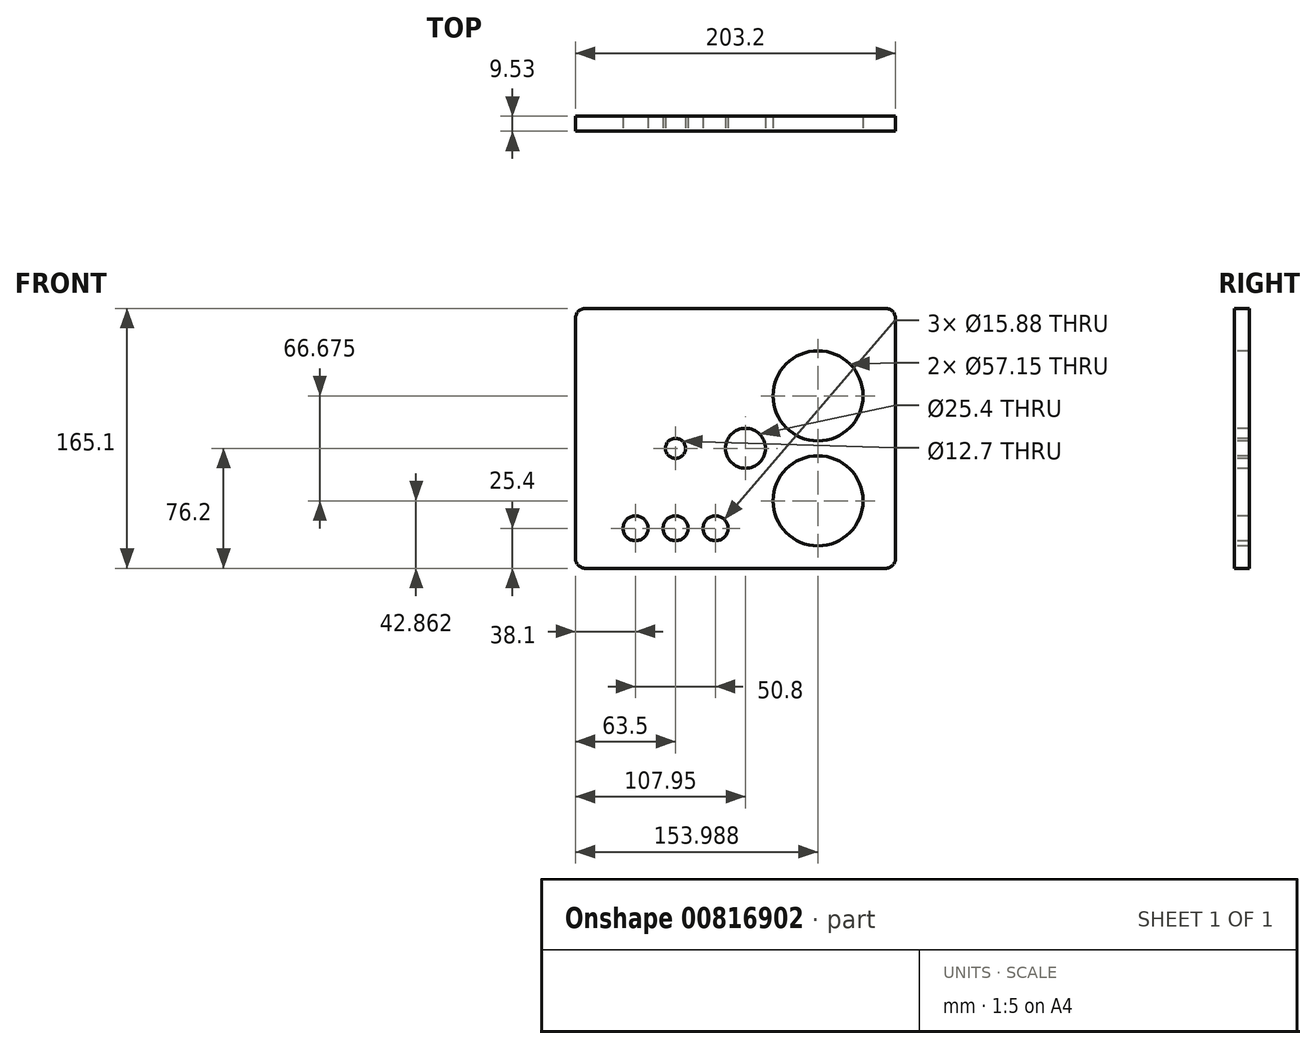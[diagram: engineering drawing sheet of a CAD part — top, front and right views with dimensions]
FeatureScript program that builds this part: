
annotation { "Feature Type Name" : "Feature", "Feature Type Description" : "" }
export const myFeature = defineFeature(function(context is Context, id is Id, definition is map)
    precondition{}
    {
        {
            var Q0;
            Q0=qCreatedBy(makeId("Front.planeOp"),FACE);
            var sketch = newSketch(context, id + "F0", { "sketchPlane" : qUnion([Q0])});
            skLineSegment(sketch, "E0.bottom", {"start": v(95.25, -82.55) * mm, "end": v(-95.25, -82.55) * mm});
            skLineSegment(sketch, "E0.top", {"start": v(95.25, 82.55) * mm, "end": v(-95.25, 82.55) * mm});
            skLineSegment(sketch, "E0.left", {"start": v(101.6, -76.2) * mm, "end": v(101.6, 76.2) * mm});
            skLineSegment(sketch, "E0.right", {"start": v(-101.6, -76.2) * mm, "end": v(-101.6, 76.2) * mm});
            skPoint(sketch, "E0.middle", {"position": v(0, 0) * mm});
            skPoint(sketch, "E1.visualSharp", {"position": v(-101.6, 82.55) * mm});
            skArc(sketch, "E1.filletArc", {"start": v(-95.25, 82.55) * mm, "mid": v(-99.74, 80.7) * mm, "end": v(-101.6, 76.2) * mm});
            skPoint(sketch, "E2.visualSharp", {"position": v(-101.6, -82.55) * mm});
            skArc(sketch, "E2.filletArc", {"start": v(-101.6, -76.2) * mm, "mid": v(-99.74, -80.7) * mm, "end": v(-95.25, -82.55) * mm});
            skPoint(sketch, "E3.visualSharp", {"position": v(101.6, -82.55) * mm});
            skArc(sketch, "E3.filletArc", {"start": v(95.25, -82.55) * mm, "mid": v(99.74, -80.7) * mm, "end": v(101.6, -76.2) * mm});
            skPoint(sketch, "E4.visualSharp", {"position": v(101.6, 82.55) * mm});
            skArc(sketch, "E4.filletArc", {"start": v(101.6, 76.2) * mm, "mid": v(99.74, 80.7) * mm, "end": v(95.25, 82.55) * mm});
            skLineSegment(sketch, "E5.bottom", {"start": v(-88.9, 44.45) * mm, "end": v(88.9, 44.45) * mm, "construction": true});
            skLineSegment(sketch, "E5.top", {"start": v(-88.9, -69.85) * mm, "end": v(88.9, -69.85) * mm, "construction": true});
            skLineSegment(sketch, "E5.left", {"start": v(-88.9, 44.45) * mm, "end": v(-88.9, -69.85) * mm, "construction": true});
            skLineSegment(sketch, "E5.right", {"start": v(88.9, 44.45) * mm, "end": v(88.9, -69.85) * mm, "construction": true});
            skSolve(sketch);
        }
        {
            var Q0;
            Q0 = qSketchRegion(id + "F0", true);
            extrude(context, id + "F1", {"entities" : qUnion([Q0]), "depth" : 9.52 * mm, "offsetDistance" : 25.4 * mm});
        }
        {
            var Q0;
            Q0=makeQuery(id+"F1.opExtrude","CAP_FACE",FACE,{"disambiguationData":[OSD([sQuery(id+"F0.wireOp",EDGE,"E0.bottom"),sQuery(id+"F0.wireOp",EDGE,"E0.top"),sQuery(id+"F0.wireOp",EDGE,"E0.left"),sQuery(id+"F0.wireOp",EDGE,"E0.right"),sQuery(id+"F0.wireOp",EDGE,"E1.filletArc"),sQuery(id+"F0.wireOp",EDGE,"E2.filletArc"),sQuery(id+"F0.wireOp",EDGE,"E3.filletArc"),sQuery(id+"F0.wireOp",EDGE,"E4.filletArc")])],"isStart":false});
            var sketch = newSketch(context, id + "F2", { "sketchPlane" : qUnion([Q0])});
            skCircle(sketch, "E6", {"center": v(52.39, -39.69) * mm, "radius": 30.16 * mm});
            skCircle(sketch, "E7", {"center": v(52.39, -39.69) * mm, "radius": 28.58 * mm});
            skCircle(sketch, "E8", {"center": v(52.39, 26.99) * mm, "radius": 30.16 * mm});
            skCircle(sketch, "E9", {"center": v(52.39, 26.99) * mm, "radius": 28.58 * mm});
            skSolve(sketch);
        }
        {
            var Q0;
            Q0=makeQuery(id+"F2.imprint","IMPRINT",FACE,{"disambiguationData":[TD([[makeQuery(id+"F2.imprint","IMPRINT",EDGE,{"derivedFrom":sQuery(id+"F2.wireOp",EDGE,"E6")}),-1.0]])]});
            var sketch = newSketch(context, id + "F3", { "sketchPlane" : qUnion([Q0])});
            skLineSegment(sketch, "E10", {"start": v(-90.38, -57.15) * mm, "end": v(29.27, -57.15) * mm, "construction": true});
            skCircle(sketch, "E11", {"center": v(-63.5, -57.15) * mm, "radius": 7.94 * mm});
            skCircle(sketch, "E12", {"center": v(-38.1, -57.15) * mm, "radius": 7.94 * mm});
            skCircle(sketch, "E13", {"center": v(-12.7, -57.15) * mm, "radius": 7.94 * mm});
            skSolve(sketch);
        }
        {
            var Q0;
            Q0=makeQuery(id+"F1.opExtrude","CAP_FACE",FACE,{"disambiguationData":[OSD([sQuery(id+"F0.wireOp",EDGE,"E0.bottom"),sQuery(id+"F0.wireOp",EDGE,"E0.top"),sQuery(id+"F0.wireOp",EDGE,"E0.left"),sQuery(id+"F0.wireOp",EDGE,"E0.right"),sQuery(id+"F0.wireOp",EDGE,"E1.filletArc"),sQuery(id+"F0.wireOp",EDGE,"E2.filletArc"),sQuery(id+"F0.wireOp",EDGE,"E3.filletArc"),sQuery(id+"F0.wireOp",EDGE,"E4.filletArc")])],"isStart":false});
            var sketch = newSketch(context, id + "F4", { "sketchPlane" : qUnion([Q0])});
            skLineSegment(sketch, "E14", {"start": v(89.12, -6.35) * mm, "end": v(-75.85, -6.35) * mm, "construction": true});
            skCircle(sketch, "E15", {"center": v(6.35, -6.35) * mm, "radius": 12.7 * mm});
            skLineSegment(sketch, "E16.bottom", {"start": v(19.05, -38.1) * mm, "end": v(-6.35, -38.1) * mm, "construction": true});
            skLineSegment(sketch, "E16.top", {"start": v(19.05, 19.05) * mm, "end": v(-6.35, 19.05) * mm, "construction": true});
            skLineSegment(sketch, "E16.left", {"start": v(19.05, -38.1) * mm, "end": v(19.05, 19.05) * mm, "construction": true});
            skLineSegment(sketch, "E16.right", {"start": v(-6.35, -38.1) * mm, "end": v(-6.35, 19.05) * mm, "construction": true});
            skSolve(sketch);
        }
        {
            var Q0;
            Q0=makeQuery(id+"F2.imprint","IMPRINT",FACE,{"disambiguationData":[TD([[makeQuery(id+"F2.imprint","IMPRINT",EDGE,{"derivedFrom":sQuery(id+"F2.wireOp",EDGE,"E6")}),-1.0]])]});
            var sketch = newSketch(context, id + "F5", { "sketchPlane" : qUnion([Q0])});
            skCircle(sketch, "E17", {"center": v(-38.1, -6.35) * mm, "radius": 6.35 * mm});
            skSolve(sketch);
        }
        {
            var Q0;
            Q0=makeQuery(id+"F2.imprint","IMPRINT",FACE,{"disambiguationData":[TD([[makeQuery(id+"F2.imprint","IMPRINT",EDGE,{"derivedFrom":sQuery(id+"F2.wireOp",EDGE,"E9")}),1.0]])]});
            var Q1;
            Q1=makeQuery(id+"F2.imprint","IMPRINT",FACE,{"disambiguationData":[TD([[makeQuery(id+"F2.imprint","IMPRINT",EDGE,{"derivedFrom":sQuery(id+"F2.wireOp",EDGE,"E7")}),1.0]])]});
            var Q2;
            Q2 = qSketchRegion(id + "F3", true);
            var Q3;
            Q3 = qSketchRegion(id + "F5", true);
            var Q4;
            Q4 = qSketchRegion(id + "F4", true);
            extrude(context, id + "F6", {"entities" : qUnion([Q0, Q1, Q2, Q3, Q4]), "operationType" : NewBodyOperationType.REMOVE, "endBound" : BoundingType.THROUGH_ALL, "oppositeDirection" : true, "depth" : 25.4 * mm, "offsetDistance" : 25.4 * mm});
        }
    });
